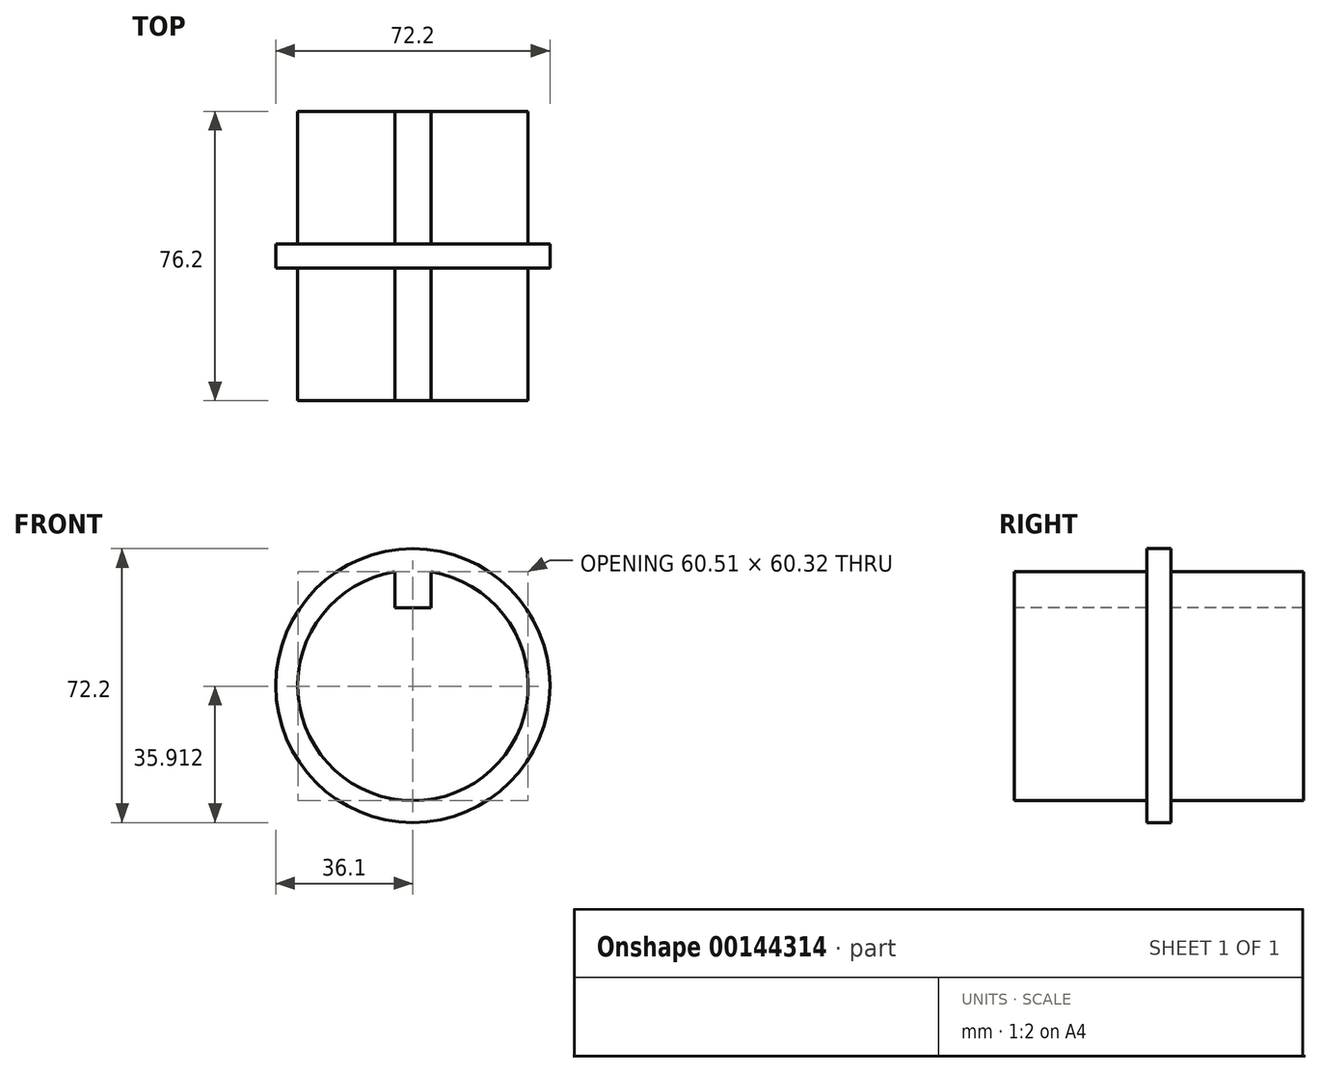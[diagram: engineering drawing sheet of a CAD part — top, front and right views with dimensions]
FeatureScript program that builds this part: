
annotation { "Feature Type Name" : "Feature", "Feature Type Description" : "" }
export const myFeature = defineFeature(function(context is Context, id is Id, definition is map)
    precondition{}
    {
        {
            var Q0;
            Q0=qCreatedBy(makeId("Front.planeOp"),FACE);
            var sketch = newSketch(context, id + "F0", { "sketchPlane" : qUnion([Q0])});
            skCircle(sketch, "E0", {"center": v(0, 0) * mm, "radius": 30.35 * mm});
            skSolve(sketch);
        }
        {
            var Q0;
            Q0 = qSketchRegion(id + "F0", true);
            extrude(context, id + "F1", {"entities" : qUnion([Q0]), "endBound" : BoundingType.SYMMETRIC, "depth" : 76.2 * mm});
        }
        {
            var Q0;
            Q0=makeQuery(id+"F1.opExtrude","CAP_FACE",FACE,{"disambiguationData":[OSD([sQuery(id+"F0.wireOp",EDGE,"E0")])],"isStart":false});
            var sketch = newSketch(context, id + "F2", { "sketchPlane" : qUnion([Q0])});
            skLineSegment(sketch, "E1.bottom", {"start": v(4.76, 40.14) * mm, "end": v(-4.76, 40.14) * mm});
            skLineSegment(sketch, "E1.top", {"start": v(4.76, 20.56) * mm, "end": v(-4.76, 20.56) * mm});
            skLineSegment(sketch, "E1.left", {"start": v(4.76, 40.14) * mm, "end": v(4.76, 20.56) * mm});
            skLineSegment(sketch, "E1.right", {"start": v(-4.76, 40.14) * mm, "end": v(-4.76, 20.56) * mm});
            skPoint(sketch, "E1.middle", {"position": v(0, 30.35) * mm});
            skSolve(sketch);
        }
        {
            var Q0;
            Q0 = qSketchRegion(id + "F2", true);
            extrude(context, id + "F3", {"entities" : qUnion([Q0]), "operationType" : NewBodyOperationType.REMOVE, "oppositeDirection" : true, "depth" : 101.6 * mm});
        }
        {
            var Q0;
            Q0=qCreatedBy(makeId("Front.planeOp"),FACE);
            var sketch = newSketch(context, id + "F4", { "sketchPlane" : qUnion([Q0])});
            skCircle(sketch, "E2", {"center": v(0, 0) * mm, "radius": 36.1 * mm});
            skSolve(sketch);
        }
        {
            var Q0;
            Q0 = qSketchRegion(id + "F4", true);
            extrude(context, id + "F5", {"entities" : qUnion([Q0]), "operationType" : NewBodyOperationType.ADD, "endBound" : BoundingType.SYMMETRIC, "depth" : 6.35 * mm});
        }
    });
